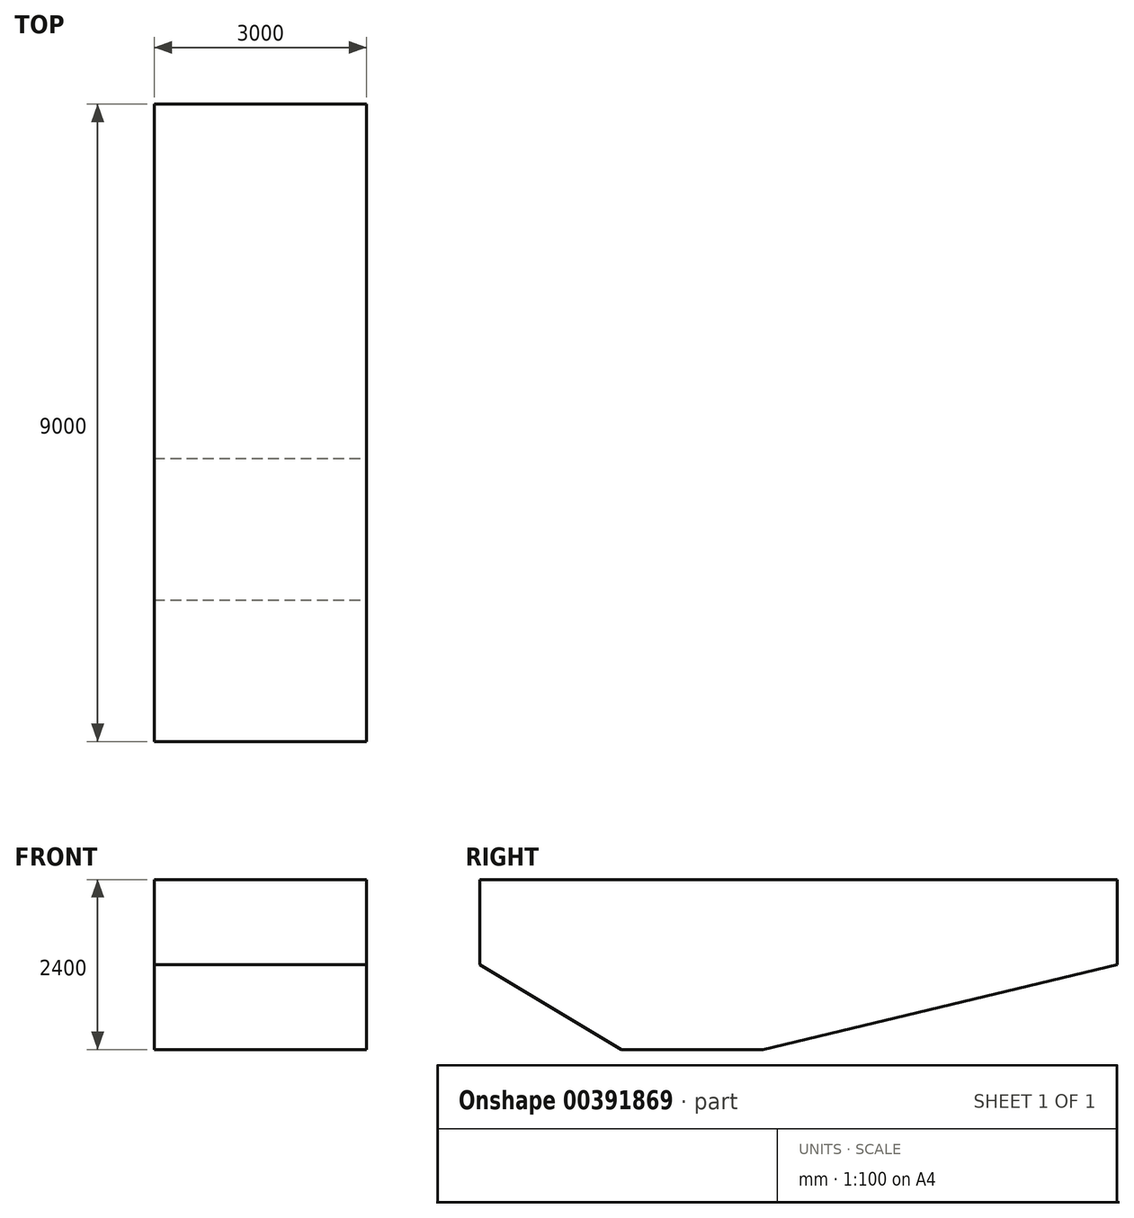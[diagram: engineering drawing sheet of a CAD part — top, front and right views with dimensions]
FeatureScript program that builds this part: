
annotation { "Feature Type Name" : "Feature", "Feature Type Description" : "" }
export const myFeature = defineFeature(function(context is Context, id is Id, definition is map)
    precondition{}
    {
        {
            var Q0;
            Q0=qCreatedBy(makeId("Top.planeOp"),FACE);
            var sketch = newSketch(context, id + "F0", { "sketchPlane" : qUnion([Q0])});
            skLineSegment(sketch, "E0.bottom", {"start": v(0, 0) * mm, "end": v(3000, 0) * mm});
            skLineSegment(sketch, "E0.top", {"start": v(0, 9000) * mm, "end": v(3000, 9000) * mm});
            skLineSegment(sketch, "E0.left", {"start": v(0, 0) * mm, "end": v(0, 9000) * mm});
            skLineSegment(sketch, "E0.right", {"start": v(3000, 0) * mm, "end": v(3000, 9000) * mm});
            skSolve(sketch);
        }
        {
            var Q0;
            Q0=makeQuery(id+"F0.imprint","IMPRINT",FACE,{"disambiguationData":[TD([[makeQuery(id+"F0.imprint","IMPRINT",EDGE,{"derivedFrom":sQuery(id+"F0.wireOp",EDGE,"E0.bottom")}),1.0]])]});
            extrude(context, id + "F1", {"entities" : qUnion([Q0]), "oppositeDirection" : true, "depth" : 2400 * mm});
        }
        {
            var Q0;
            Q0=makeQuery(id+"F1.opExtrude","SWEPT_FACE",FACE,{"disambiguationData":[OSD([sQuery(id+"F0.wireOp",EDGE,"E0.right")])]});
            var sketch = newSketch(context, id + "F2", { "sketchPlane" : qUnion([Q0])});
            skLineSegment(sketch, "E1", {"start": v(0, -2400) * mm, "end": v(0, -1200) * mm});
            skLineSegment(sketch, "E2", {"start": v(0, -1200) * mm, "end": v(2000, -2400) * mm});
            skLineSegment(sketch, "E3", {"start": v(2000, -2400) * mm, "end": v(0, -2400) * mm});
            skLineSegment(sketch, "E4", {"start": v(9000, -2400) * mm, "end": v(9000, -1200) * mm});
            skLineSegment(sketch, "E5", {"start": v(9000, -1200) * mm, "end": v(4000, -2400) * mm});
            skLineSegment(sketch, "E6", {"start": v(4000, -2400) * mm, "end": v(9000, -2400) * mm});
            skSolve(sketch);
        }
        {
            var Q0;
            Q0=makeQuery(id+"F2.imprint","IMPRINT",FACE,{"disambiguationData":[TD([[makeQuery(id+"F2.imprint","IMPRINT",EDGE,{"derivedFrom":sQuery(id+"F2.wireOp",EDGE,"E1")}),-1.0]])]});
            var Q1;
            Q1=makeQuery(id+"F2.imprint","IMPRINT",FACE,{"disambiguationData":[TD([[makeQuery(id+"F2.imprint","IMPRINT",EDGE,{"derivedFrom":sQuery(id+"F2.wireOp",EDGE,"E4")}),1.0]])]});
            extrude(context, id + "F3", {"entities" : qUnion([Q0, Q1]), "operationType" : NewBodyOperationType.REMOVE, "endBound" : BoundingType.THROUGH_ALL, "oppositeDirection" : true, "depth" : 25 * mm});
        }
    });
